# Revit family: IS_Idealrain_B9503_BIM_BE
name_source: partatom
category: Plumbing Fixtures
revit_build: Autodesk Revit 2015 (Build: 20140606_1530(x64)
units: mm (PartAtom-declared; Revit-internal decimal feet)

## types (1)
- B9503AA - Idealrain Barre de douche 600 mm avec douchette 80 mm avec 3 fonctions
    Accesoires = www.idealstandard.be
    Afwerking = Chroom
    Auteur = Ideal Standard Produktions-GmbH
    Barcode = 3800861023814
    Beschrijvinggarantie = Fabrieksgarantie
    BimObjectNaam = ISI_IdealStandard_Douche_Idealrain_B9503AA
    Breedte = 0
    BrutoGewicht = 0
    Cost = 0 $
    Debiet = 8L/min | 3bar
    Default Elevation = 1219 mm
    Description = Idealrain Barre de douche 600 mm avec douchette 80 mm avec 3 fonctions
    Diepte = 0 mm  [stored 0 ft]
    Dimensions = 184 x 145 x 610 mm
    DuurEenheid = jaar
    Eigenschappen = IdealRain glijstangcombinatie van 600mm, met transparante zeepschaal, handdouche 80 mm in verchroomd ABS. 8 l/min. met 3 functies, Metalflex 1750 mm.
    Garantieonderdelen = 2
    Hauteur = 609 mm
    IfcExportAs = IfcValveTypes
    IfcExportType = SHOWERS
    Installatieinstructies = www.idealstandard.be
    Kleur = Chroom
    Largeur = 145 mm
    Lengte = 0 mm  [stored 0 ft]
    Longueur = 184 mm
    Manufacturer = www.idealstandard.be
    Materiaal = messing verchroomd
    Merk = Ideal Standard
    Model = B9503AA
    Nettogewicht = 1.1
    Productinformatie = www.idealstandard.be
    Telefoonnummer = 0032 2 325 66 00
    Testdruk = 10 bar
    Typeconnectie = Sanitair
    URL = www.idealstandard.be
    Uniclass2015Beschrijving = Douche
    Uniclass2015Version = Products v1.1
    Urlproducent = www.idealstandard.be
    Versie = 1
    Vervangingskosten = 0
    Verwachtelevensduur = 25 jaar
    Volumeunits = liter
    Werkdruk = 1-5 bar

note: [stored X ft] marks values corroborated as IEEE doubles in the binary element streams (Revit-internal decimal feet)

## geometry (parser evidence)
native form markers: Blend x2, Sweep x3
no freeform markers — native parametric forms only
